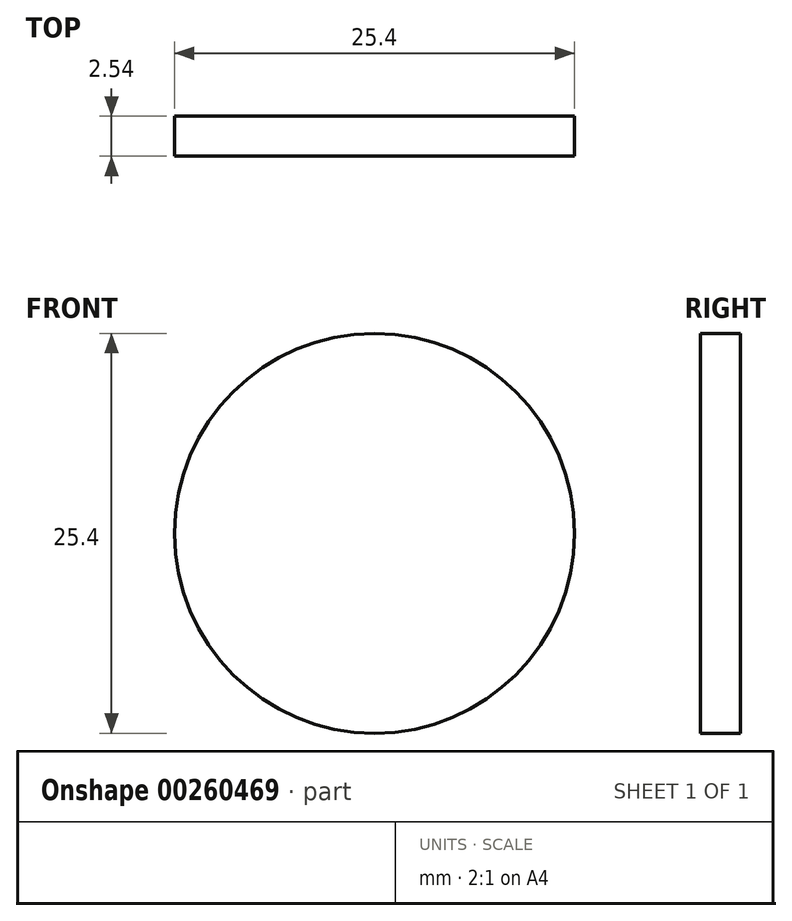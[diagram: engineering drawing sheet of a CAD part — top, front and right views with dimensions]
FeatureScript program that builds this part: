
annotation { "Feature Type Name" : "Feature", "Feature Type Description" : "" }
export const myFeature = defineFeature(function(context is Context, id is Id, definition is map)
    precondition{}
    {
        {
            var Q0;
            Q0=qCreatedBy(makeId("Front.planeOp"),FACE);
            var sketch = newSketch(context, id + "F0", { "sketchPlane" : qUnion([Q0])});
            skCircle(sketch, "E0", {"center": v(0, 0) * mm, "radius": 12.7 * mm});
            skSolve(sketch);
        }
        {
            var Q0;
            Q0=makeQuery(id+"F0.imprint","IMPRINT",FACE,{"disambiguationData":[TD([[makeQuery(id+"F0.imprint","IMPRINT",EDGE,{"derivedFrom":sQuery(id+"F0.wireOp",EDGE,"E0")}),1.0]])]});
            extrude(context, id + "F1", {"entities" : qUnion([Q0]), "depth" : 2.54 * mm});
        }
    });
